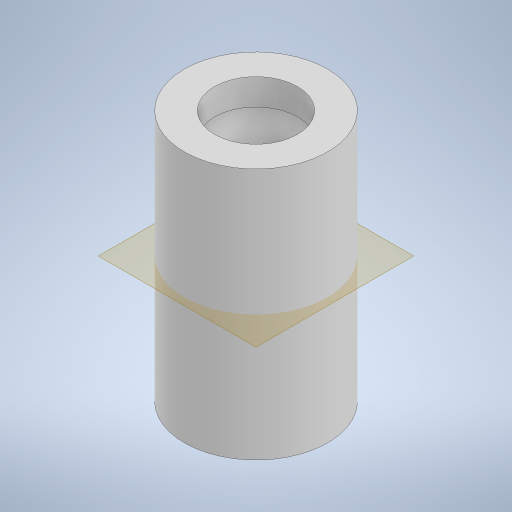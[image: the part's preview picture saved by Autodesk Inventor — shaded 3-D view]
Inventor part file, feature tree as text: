
AUTODESK INVENTOR PART (.ipt)
format: ipt  version: 2024 (Build 280153020, 153B)  size: 362,496 bytes
history: native  units: in
note: dims shown in document units (in); Inventor stores cm internally (conversion verified against a paired STEP export)
features: sketch x6, plane x4, extrude x2, loft x1, mirror x1
ambient origin geometry x8: Origin, YZ Plane, XZ Plane, XY Plane, X Axis, Y Axis, Z Axis, Center Point
bodies: Solid1 (feature_tree)
feature tree (14):
  extrude  "Extrusion1"  Depth=2.6378in TaperAngle=0.0deg
  extrude  "Extrusion2"  Depth=0.2756in TaperAngle=0.0deg
  plane  "Work Plane1"
  plane  "Work Plane2"
  sketch  "Sketch4"  dims[d6=-0.5906in d7=1.1in]
  sketch  "Sketch5"  dims[d8=0.1969in]
  plane  "Work Plane3"
  plane  "Work Plane4"
  loft  "Loft1"
  mirror  "Mirror1"
  sketch  "Sketch1"  dims[d0=1.5in d1=2.6378in d2=0.0in]
  sketch  "Sketch2"  dims[d3=0.8681in d4=0.2756in d5=0.0in]
  sketch  "Sketch8"  dims[d10=-0.1969in]
  sketch  "Sketch9"  dims[d11=0.748in d12=1.1in d13=0.0in d14=90.0deg d15=0.0in d16=90.0deg d17=0.0in d18=90.0deg d19=0.0in d20=90.0deg]
